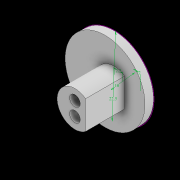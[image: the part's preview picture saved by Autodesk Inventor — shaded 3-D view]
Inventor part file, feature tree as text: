
AUTODESK INVENTOR PART (.ipt)
format: ipt  version: 2022.2 (Build 262287010, 287A)  size: 115,712 bytes
history: native  units: mm
features: sketch x3, extrude x3, hole x1, draft x1, plane x1
ambient origin geometry x8: Origin, YZ Plane, XZ Plane, XY Plane, X Axis, Y Axis, Z Axis, Center Point
bodies: Solid1 (feature_tree)
feature tree (9):
  sketch  "Sketch1"  dims[d0=22.5mm d1=2.5mm]
  extrude  "Extrusion1"  Depth=2.5mm
  extrude  "Extrusion2"  Depth=10.0mm
  hole  "Hole1"  [1 undecoded]
  draft  "FaceDraft1"
  plane  "Work Plane1"
  extrude  "Extrusion3"  Depth=4.0mm
  sketch  "Sketch2"  dims[d2=10.0mm d3=2.0mm]
  sketch  "Sketch3"  dims[d4=2.5mm d5=0.0mm d6=11.0mm d7=0.0mm d8=2.0mm d9=2.0mm d10=3.0mm d11=6.0mm d12=4.0mm d13=2.0mm d14=90.0deg d15=4.0mm d16=0.0mm d17=20.0mm d18=25.0mm d19=25.0mm d20=2.0mm d21=0.0mm d22=0.436332mm]
note: 1 required parameter value undecoded (feature->parameter linkage not recoverable at this tier; creation-order binding heuristic only, values carry confidence <= 0.55)
